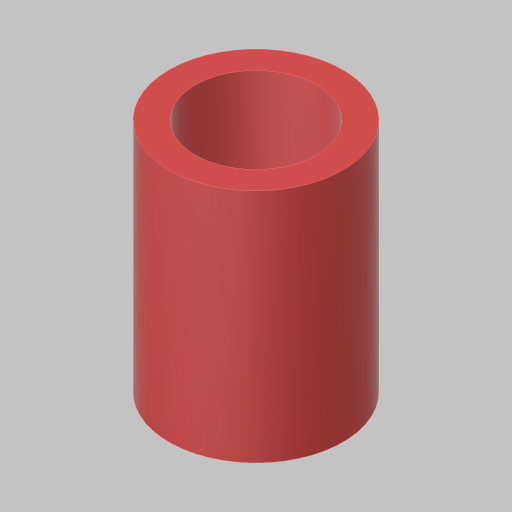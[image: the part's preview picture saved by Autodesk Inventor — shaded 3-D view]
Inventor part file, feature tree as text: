
AUTODESK INVENTOR PART (.ipt)
format: ipt  version: 2023.5 (Build 275446000, 446)  size: 103,936 bytes
history: native  units: in
note: dims shown in document units (in); Inventor stores cm internally (conversion verified against a paired STEP export)
features: extrude x1, sketch x1
ambient origin geometry x8: Origin, YZ Plane, XZ Plane, XY Plane, X Axis, Y Axis, Z Axis, Center Point
bodies: Solid1 (feature_tree)
feature tree (2):
  extrude  "Extrusion1"  Depth=1.125in
  sketch  "Sketch1"  dims[d0=0.58in d1=0.125in d2=1.125in d3=0.0in]
